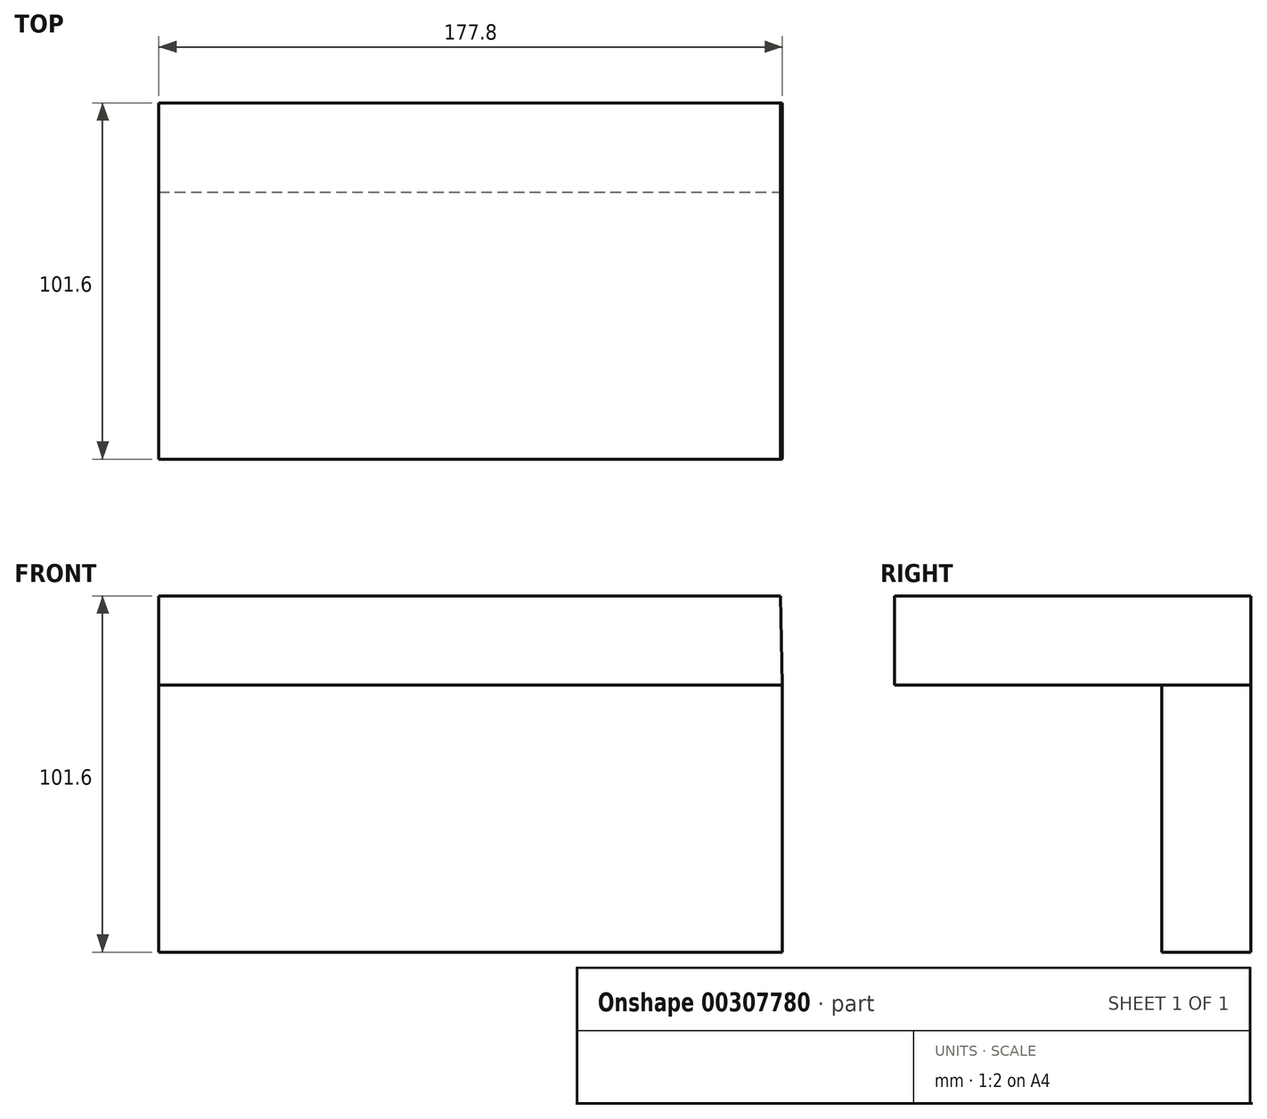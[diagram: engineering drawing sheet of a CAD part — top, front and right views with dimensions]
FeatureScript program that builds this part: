
annotation { "Feature Type Name" : "Feature", "Feature Type Description" : "" }
export const myFeature = defineFeature(function(context is Context, id is Id, definition is map)
    precondition{}
    {
        {
            var Q0;
            Q0=qCreatedBy(makeId("Front.planeOp"),FACE);
            var sketch = newSketch(context, id + "F0", { "sketchPlane" : qUnion([Q0])});
            skLineSegment(sketch, "E0.bottom", {"start": v(-85.44, 38.42) * mm, "end": v(92.36, 38.42) * mm});
            skLineSegment(sketch, "E0.top", {"start": v(-85.44, -37.78) * mm, "end": v(92.36, -37.78) * mm});
            skLineSegment(sketch, "E0.left", {"start": v(-85.44, 38.42) * mm, "end": v(-85.44, -37.78) * mm});
            skLineSegment(sketch, "E0.right", {"start": v(92.36, 38.42) * mm, "end": v(92.36, -37.78) * mm});
            skLineSegment(sketch, "E1", {"start": v(-85.44, 38.42) * mm, "end": v(-85.44, 63.82) * mm});
            skLineSegment(sketch, "E2", {"start": v(-85.44, 63.82) * mm, "end": v(91.83, 63.82) * mm});
            skLineSegment(sketch, "E3", {"start": v(91.83, 63.82) * mm, "end": v(92.36, 38.42) * mm});
            skSolve(sketch);
        }
        {
            var Q0;
            Q0=makeQuery(id+"F0.imprint","IMPRINT",FACE,{"disambiguationData":[TD([[makeQuery(id+"F0.imprint","IMPRINT",EDGE,{"derivedFrom":sQuery(id+"F0.wireOp",EDGE,"E0.bottom")}),-1.0]])]});
            extrude(context, id + "F1", {"entities" : qUnion([Q0]), "depth" : 25.4 * mm});
        }
        {
            var Q0;
            Q0=makeQuery(id+"F0.imprint","IMPRINT",FACE,{"disambiguationData":[TD([[makeQuery(id+"F0.imprint","IMPRINT",EDGE,{"derivedFrom":sQuery(id+"F0.wireOp",EDGE,"E0.bottom")}),1.0]])]});
            extrude(context, id + "F2", {"entities" : qUnion([Q0]), "operationType" : NewBodyOperationType.ADD, "depth" : 101.6 * mm});
        }
    });
